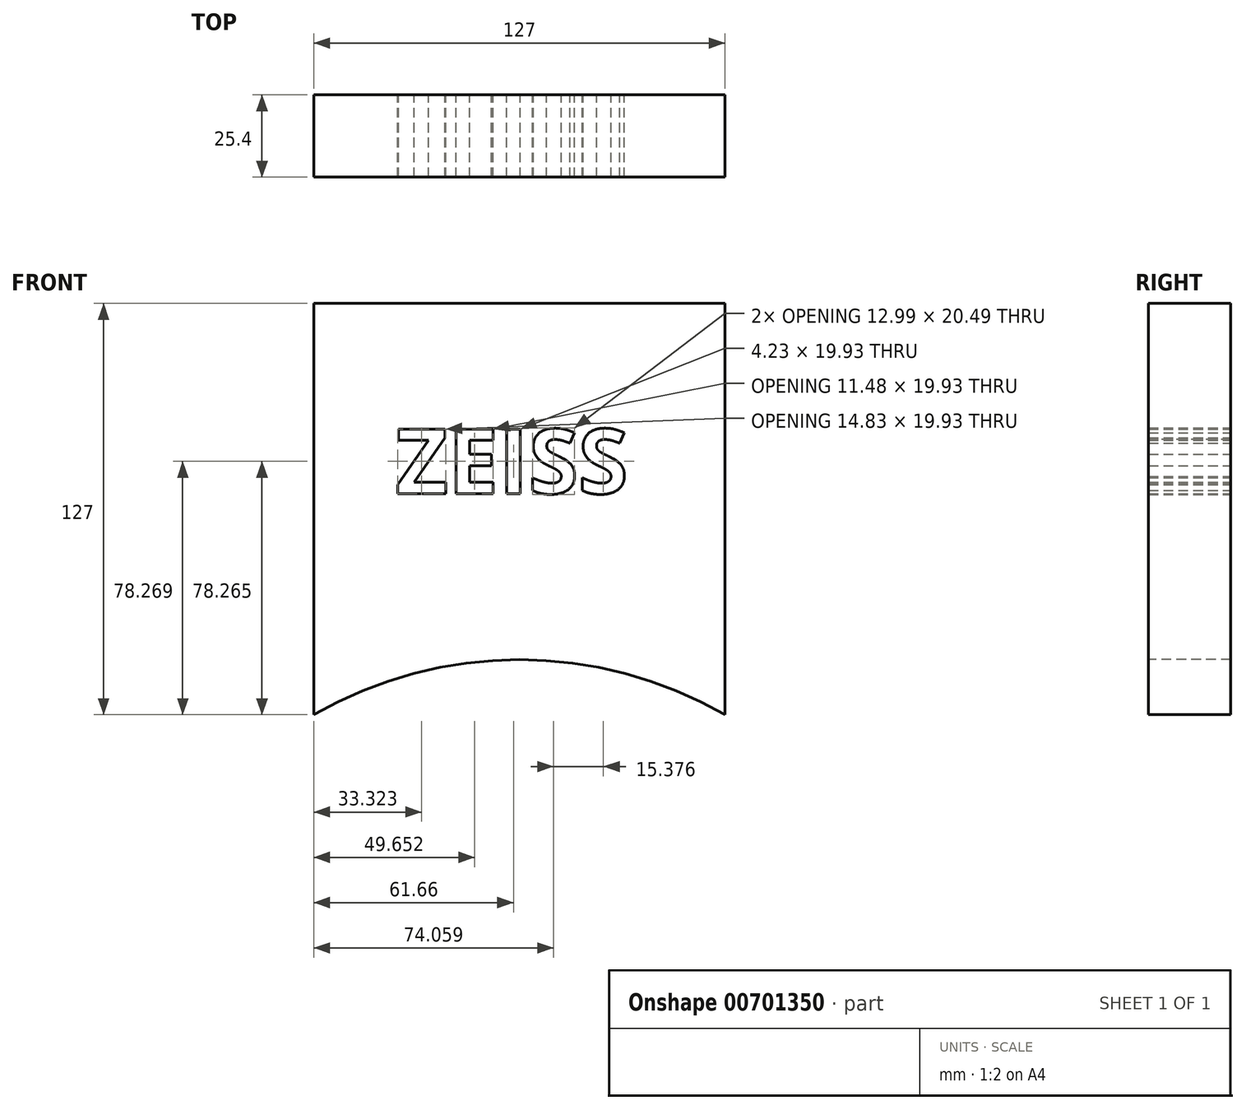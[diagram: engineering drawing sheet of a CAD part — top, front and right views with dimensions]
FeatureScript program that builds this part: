
annotation { "Feature Type Name" : "Feature", "Feature Type Description" : "" }
export const myFeature = defineFeature(function(context is Context, id is Id, definition is map)
    precondition{}
    {
        {
            var Q0;
            Q0=qCreatedBy(makeId("Front.planeOp"),FACE);
            var sketch = newSketch(context, id + "F0", { "sketchPlane" : qUnion([Q0])});
            skLineSegment(sketch, "E0.bottom", {"start": v(63.5, 63.5) * mm, "end": v(-63.5, 63.5) * mm});
            skLineSegment(sketch, "E0.top", {"start": v(63.5, -63.5) * mm, "end": v(-63.5, -63.5) * mm});
            skLineSegment(sketch, "E0.left", {"start": v(63.5, 63.5) * mm, "end": v(63.5, -63.5) * mm});
            skLineSegment(sketch, "E0.right", {"start": v(-63.5, 63.5) * mm, "end": v(-63.5, -63.5) * mm});
            skPoint(sketch, "E0.middle", {"position": v(0, 0) * mm});
            skText(sketch, "E1", { "text": "ZEISS", "fontName": "OpenSans-Bold.ttf"});
            const initialGuessF0  = {"E1": [-0.03826, 0.0048, 1, 0, 0.0201]};
            skSetInitialGuess(sketch, initialGuessF0);
            skSolve(sketch);
        }
        {
            var Q0;
            Q0 = qSketchRegion(id + "F0", true);
            extrude(context, id + "F1", {"entities" : qUnion([Q0]), "depth" : 25.4 * mm, "offsetDistance" : 25.4 * mm});
        }
        {
            var Q0;
            Q0=makeQuery(id+"F1.opExtrude","CAP_FACE",FACE,{"disambiguationData":[OSD([sQuery(id+"F0.wireOp",EDGE,"E0.bottom"),sQuery(id+"F0.wireOp",EDGE,"E0.top"),sQuery(id+"F0.wireOp",EDGE,"E0.left"),sQuery(id+"F0.wireOp",EDGE,"E0.right")])],"isStart":false});
            var sketch = newSketch(context, id + "F2", { "sketchPlane" : qUnion([Q0])});
            skArc(sketch, "E2", {"start": v(63.5, -63.5) * mm, "mid": v(0, -46.49) * mm, "end": v(-63.5, -63.5) * mm});
            skSolve(sketch);
        }
        {
            var Q0;
            Q0=makeQuery(id+"F2.imprint","IMPRINT",FACE,{"disambiguationData":[TD([[makeQuery(id+"F2.imprint","IMPRINT",EDGE,{"derivedFrom":sQuery(id+"F2.wireOp",EDGE,"E2")}),1.0]])]});
            extrude(context, id + "F3", {"entities" : qUnion([Q0]), "operationType" : NewBodyOperationType.REMOVE, "oppositeDirection" : true, "depth" : 25.4 * mm, "offsetDistance" : 25.4 * mm});
        }
    });
